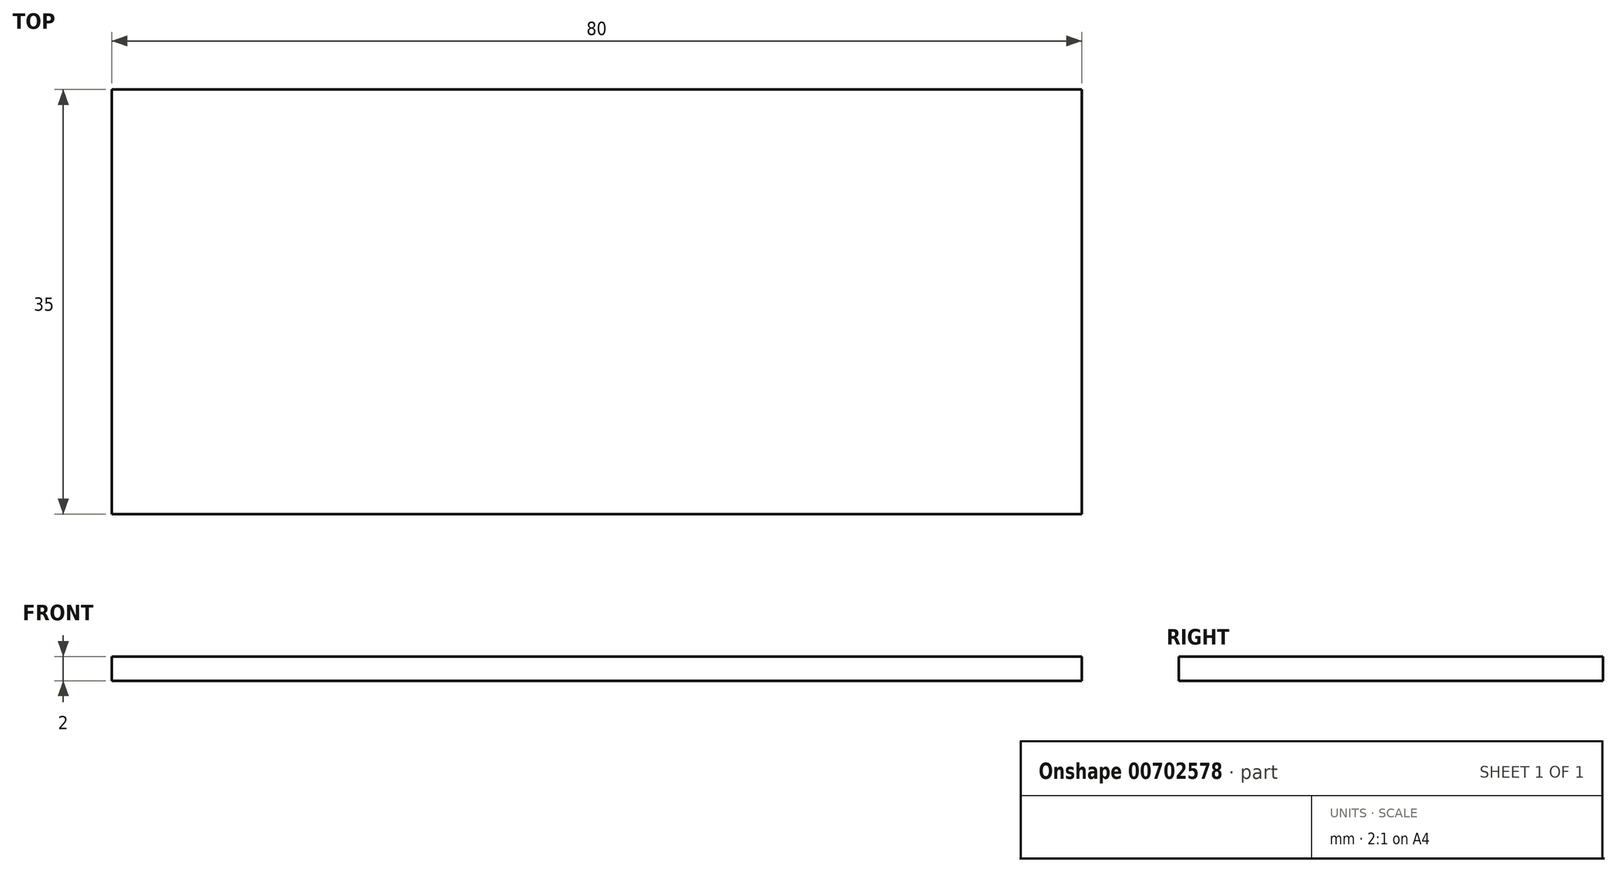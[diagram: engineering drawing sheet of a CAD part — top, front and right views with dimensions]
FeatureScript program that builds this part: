
annotation { "Feature Type Name" : "Feature", "Feature Type Description" : "" }
export const myFeature = defineFeature(function(context is Context, id is Id, definition is map)
    precondition{}
    {
        {
            var Q0;
            Q0=qCreatedBy(makeId("Top.planeOp"),FACE);
            var sketch = newSketch(context, id + "F0", { "sketchPlane" : qUnion([Q0])});
            skLineSegment(sketch, "E0.bottom", {"start": v(40, 17.5) * mm, "end": v(-40, 17.5) * mm});
            skLineSegment(sketch, "E0.top", {"start": v(40, -17.5) * mm, "end": v(-40, -17.5) * mm});
            skLineSegment(sketch, "E0.left", {"start": v(40, 17.5) * mm, "end": v(40, -17.5) * mm});
            skLineSegment(sketch, "E0.right", {"start": v(-40, 17.5) * mm, "end": v(-40, -17.5) * mm});
            skPoint(sketch, "E0.middle", {"position": v(0, 0) * mm});
            skSolve(sketch);
        }
        {
            var Q0;
            Q0 = qSketchRegion(id + "F0", true);
            extrude(context, id + "F1", {"entities" : qUnion([Q0]), "depth" : 2 * mm, "offsetDistance" : 25 * mm});
        }
    });
